# Revit family: VPS
name_source: partatom
category: Lighting Fixtures
revit_build: Autodesk Revit 2014 (Build: 20130308_1515(x64)
units: mm (PartAtom-declared; Revit-internal decimal feet)

## types (1)
- VP-S-24E2-45-AMB-2
    Apparent Load = 0 VA
    Application = Parking Area, Site Lighting
    Controls = On/Off
Scheduled Dimming
Luminaire Grouping
Occupancy Detection
Dusk-to-Dawn Operation
Lumen Maintenance Compensation
    Default Elevation = 48.000"
    Description = The Small Viper luminaire is available with a wide choice of different LED wattage configurations and optical distributions designed to replace HID lighting up to 400W MH or HPS. 4 different mounting options allow for application in a wide variety of new and existing installations.
    Finish = Basic Black Textured
    Head = Head : Small
    Height = 5.500"
    Industry Standards = CSA C/US Listed
    Lamp = LED
    Length = 22.750"
    Manufacturer = Beacon Lighting
    Model = Viper Small Strike Optic
    Pivot Angle = 0.00°
    Pivot calc. = 90.00°
    Product Documentation Link = https://hubbellcdn.com
    Product Page URL = https://www.hubbell.com
    Sensor Type = Passive Infrared with Photoresistor
    URL = https://www.hubbell.com
    Voltage = 120 V
    Warranty = 5 year limited warranty

## geometry (parser evidence)
native form markers: Blend x27, Sweep x5
no freeform markers — native parametric forms only
